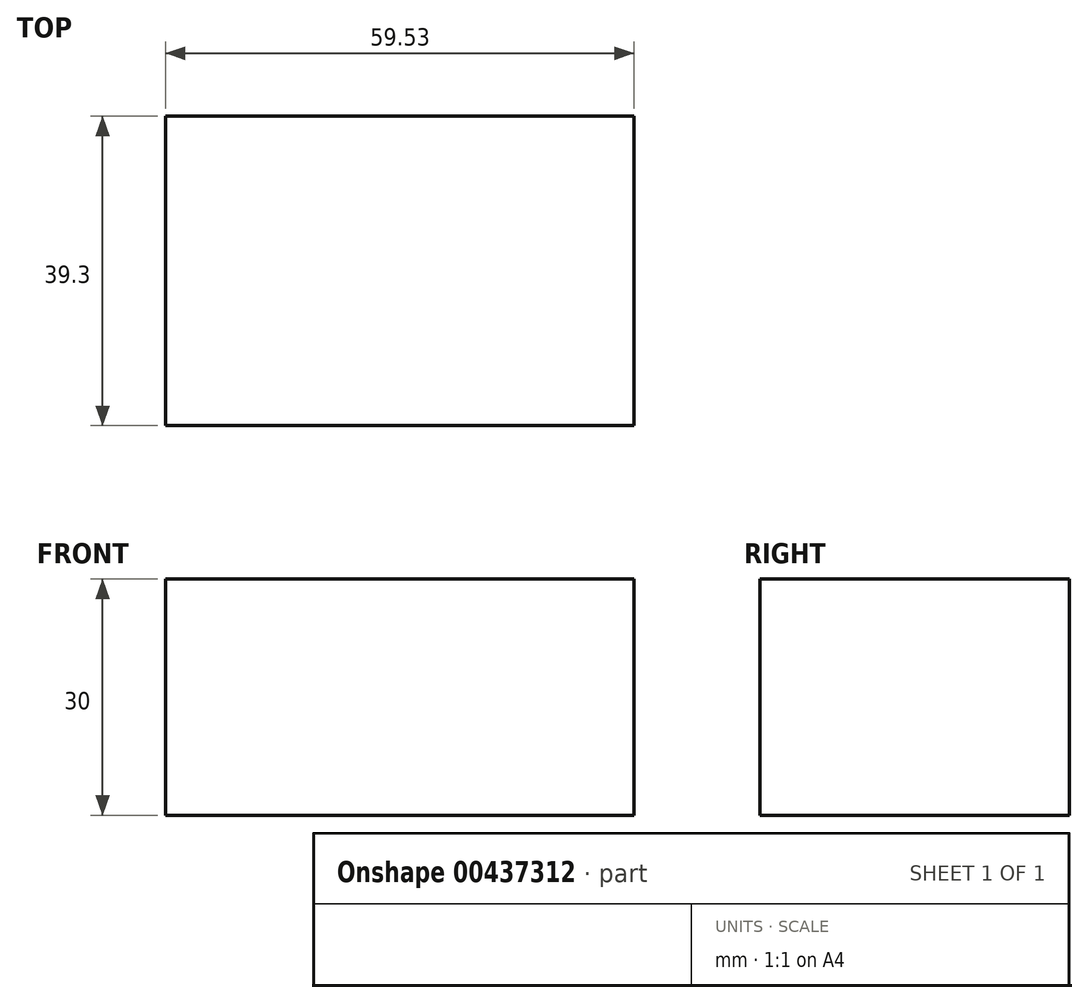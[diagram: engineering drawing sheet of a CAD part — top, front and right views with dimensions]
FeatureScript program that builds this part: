
annotation { "Feature Type Name" : "Feature", "Feature Type Description" : "" }
export const myFeature = defineFeature(function(context is Context, id is Id, definition is map)
    precondition{}
    {
        {
            var Q0;
            Q0=qCreatedBy(makeId("Top.planeOp"),FACE);
            var sketch = newSketch(context, id + "F0", { "sketchPlane" : qUnion([Q0])});
            skLineSegment(sketch, "E0.bottom", {"start": v(-19.36, 20.08) * mm, "end": v(40.17, 20.08) * mm});
            skLineSegment(sketch, "E0.top", {"start": v(-19.36, -19.22) * mm, "end": v(40.17, -19.22) * mm});
            skLineSegment(sketch, "E0.left", {"start": v(-19.36, 20.08) * mm, "end": v(-19.36, -19.22) * mm});
            skLineSegment(sketch, "E0.right", {"start": v(40.17, 20.08) * mm, "end": v(40.17, -19.22) * mm});
            skSolve(sketch);
        }
        {
            var Q0;
            Q0=makeQuery(id+"F0.imprint","IMPRINT",FACE,{"disambiguationData":[TD([[makeQuery(id+"F0.imprint","IMPRINT",EDGE,{"derivedFrom":sQuery(id+"F0.wireOp",EDGE,"E0.bottom")}),-1.0]])]});
            extrude(context, id + "F1", {"entities" : qUnion([Q0]), "depth" : 30 * mm});
        }
    });
